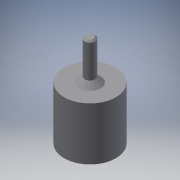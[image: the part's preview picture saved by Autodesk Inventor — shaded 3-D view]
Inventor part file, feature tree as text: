
AUTODESK INVENTOR PART (.ipt)
format: ipt  version: 2016 (Build 200138000, 138)  size: 115,712 bytes
history: native  units: mm
features: extrude x3, chamfer x3, sketch x3, reference x3, projected_geometry x1
ambient origin geometry x8: Origin, YZ Plane, XZ Plane, XY Plane, X Axis, Y Axis, Z Axis, Center Point
bodies: Solid1 (feature_tree)
feature tree (13):
  extrude  "Extrusion1"  Depth=20.0mm TaperAngle=0.0deg
  extrude  "Extrusion2"  Depth=15.0mm TaperAngle=0.0deg
  extrude  "Extrusion3"  Depth=2.0mm TaperAngle=45.0deg
  chamfer  "Chamfer1"  Distance=2.0mm Angle=45.0deg
  chamfer  "Chamfer2"  [1 undecoded]
  chamfer  "Chamfer3"  [1 undecoded]
  sketch  "Sketch1"  dims[d0=2.4mm d1=20.0mm d2=0.0mm]
  reference  "Reference1"
  sketch  "Sketch2"  dims[d3=3.0mm d4=0.0mm d5=15.0mm d6=0.0mm]
  projected_geometry  "Projected Loop1"
  reference  "Reference2"
  sketch  "Sketch3"  dims[d7=2.0mm d8=2.0mm d9=45.0deg d10=0.6mm d11=2.0mm d12=45.0deg d13=7.39mm d14=2.0mm d15=45.0deg]
  reference  "Reference3"
note: 2 required parameter values undecoded (feature->parameter linkage not recoverable at this tier; creation-order binding heuristic only, values carry confidence <= 0.55)
